# Revit family: Basketball_Backstop-Ceiling_Mount-Side_Fold-IPIbyBison-IP1345SF
name_source: partatom
category: Specialty Equipment
units: mm (PartAtom-declared; Revit-internal decimal feet)

## family parameters
Always vertical = Yes
Cut with Voids When Loaded = No
Maintain Annotation Orientation = No
OmniClass Number = 23.40.50.34.14
OmniClass Title = Gymnasium Equipment
Part Type = Normal
Room Calculation Point = No
Round Connector Dimension = Use Diameter
Shared = No

## types (2) — shared parameters
Available Options = as Specified
Backboard Type = Backboard_BA42XLGlass
CAD Details = https://www.arcat.com
Default Elevation = 0' - 0"
Description = Back Folding Basketball Frame and Backboard, Ceiling Mount
Keynote = 11 66 00
Manufacturer = IPI by Bison
Product Page URL = https://www.arcat.com
Specification = https://www.arcat.com
URL = https://ipibybison.com

## per-type parameters (varying)
| type | Fold Left | Fold Right | Model |
| Right Fold | No | Yes | IP1345SFR |
| Left Fold | Yes | No | IP1345SFL |

## geometry (parser evidence)
native form markers: Sweep x6
no freeform markers — native parametric forms only
